# Revit family: Flush-Valve-Commercial_TET3LN_TOTO
name_source: partatom
category: Plumbing Fixtures
revit_build: Autodesk Revit Architecture 2013 (Build: 20130531_2115(x64)
units: mm (PartAtom-declared; Revit-internal decimal feet)

## types (3) — shared parameters
04 CSI = 22 42 13
95 CSI = 15410
ADA Compliant = Yes
Assembly Code = D2010210
CAD Drawing URL = http://assets.totousa.com
CW Connection = Yes
Certifications = IAPMO(cUPC), State of Massachusetts, City of Los Angeles
Code Compliance = UPC, IPC, NSPC, NPC Canada, and others
Cold Water Connection NPT Radius = 0' - 0 1/2"
Color Availability = #SS Stainless Steel
Default Elevation = 1' - 11 1/2"
Depth = 0' - 6 1/2"
Finish = Metal - TOTO - Stainless Steel
Gallons Per Flush = 1.28 gal
HW Connection = No
Height = 0' - 5"
Industry Standards = Meets and exceeds ASME A112.19.2/CSA B45.1
Manufacturer = TOTO USA, Inc.
Manufacturer Fax = (770) 282-0002
Material = Bronze casting
Method of Operation = Automatic Flush
Mount Type = Concealed
Plumbing Fixture Type = Flushometer Valve
Sensor Detection Range = Self-adjusting to environment
Sensor Detection Time = Factory setting at six (6) seconds minimum
Shipping Weight = 0.00 lb
Spec Sheet URL = http://assets.totousa.com
Style = Commercial
Subcategory = Flush Valves
Toto BIM Number = BM-00257
URL = http://www.totousa.com
Vent Connection = Yes
Warranty = Three Year Warranty
Warranty URL = http://www.totousa.com
Waste Connection = Yes
Waste Connection NPT Radius = 0' - 1"
Width = 0' - 5"
zero-valued in all types: CWFU, HWFU, WFU

## per-type parameters (varying)
| type | Description |
| TET3LN31 | Sensor Toilet Flush Valve, Concealed 4 x 4" (Back Spud Wall) - 1.28 GPF" |
| TET3LN32 | Sensor Toilet Flush Valve, Concealed 4 x 4" (Top Spud) - 1.28 GPF" |
| TET3LN33 | Sensor Toilet Flush Valve, Concealed 4 x 4" (Back Spud Floor) - 1.28 GPF" |

note: column(s) folded — value = type name in every type: Model

## geometry (parser evidence)
native form markers: Blend x21, Sweep x1
no freeform markers — native parametric forms only
